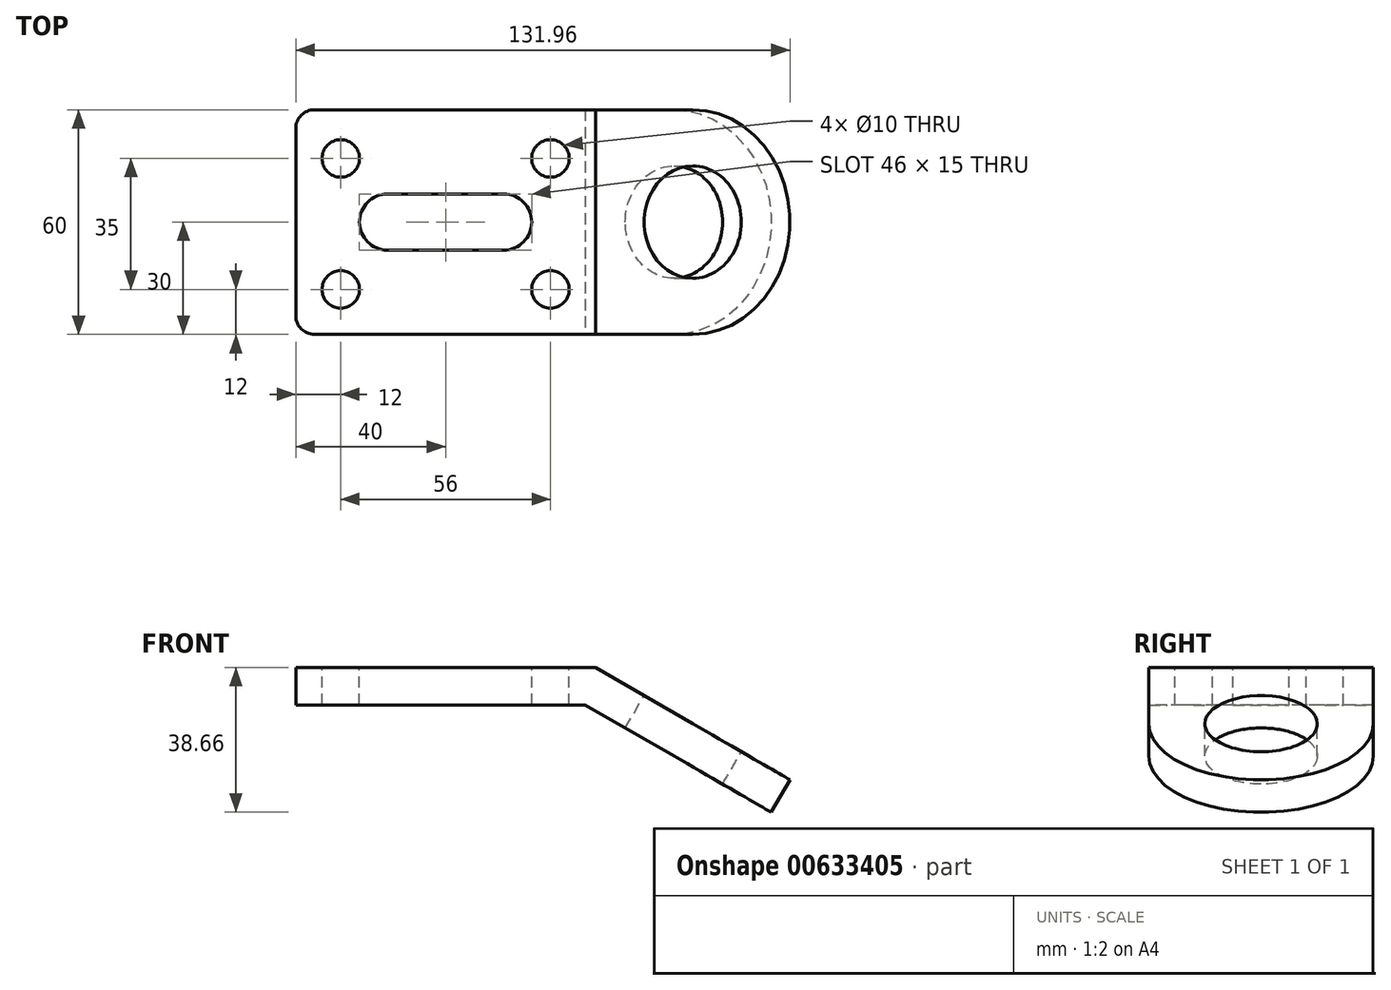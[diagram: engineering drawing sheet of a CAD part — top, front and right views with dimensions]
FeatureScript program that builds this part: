
annotation { "Feature Type Name" : "Feature", "Feature Type Description" : "" }
export const myFeature = defineFeature(function(context is Context, id is Id, definition is map)
    precondition{}
    {
        {
            var Q0;
            Q0=qCreatedBy(makeId("Front.planeOp"),FACE);
            var sketch = newSketch(context, id + "F0", { "sketchPlane" : qUnion([Q0])});
            skLineSegment(sketch, "E0", {"start": v(0, 0) * mm, "end": v(80, 0) * mm});
            skLineSegment(sketch, "E1", {"start": v(80, 0) * mm, "end": v(131.96, -30) * mm});
            skLineSegment(sketch, "E2.0", {"start": v(77.32, -10) * mm, "end": v(126.96, -38.66) * mm});
            skLineSegment(sketch, "E2.1", {"start": v(0, -10) * mm, "end": v(77.32, -10) * mm});
            skLineSegment(sketch, "E3", {"start": v(0, 0) * mm, "end": v(0, -10) * mm});
            skLineSegment(sketch, "E4", {"start": v(131.96, -30) * mm, "end": v(126.96, -38.66) * mm});
            skSolve(sketch);
        }
        {
            var Q0;
            Q0=makeQuery(id+"F0.imprint","IMPRINT",FACE,{"disambiguationData":[TD([[makeQuery(id+"F0.imprint","IMPRINT",EDGE,{"derivedFrom":sQuery(id+"F0.wireOp",EDGE,"E0")}),-1.0]])]});
            extrude(context, id + "F1", {"entities" : qUnion([Q0]), "oppositeDirection" : true, "depth" : 60 * mm, "offsetDistance" : 25 * mm});
        }
        {
            var Q0;
            Q0=makeQuery(id+"F1.opExtrude","CAP_EDGE",EDGE,{"disambiguationData":[OSD([sQuery(id+"F0.wireOp",EDGE,"E4")])],"isStart":false});
            var Q1;
            Q1=makeQuery(id+"F1.opExtrude","CAP_EDGE",EDGE,{"disambiguationData":[OSD([sQuery(id+"F0.wireOp",EDGE,"E4")])],"isStart":true});
            fillet(context, id + "F2", {"entities" : qUnion([Q0, Q1]), "radius" : 30 * mm, "tangentPropagation" : true, "allowEdgeOverflow" : false});
        }
        {
            var Q0;
            Q0=makeQuery(id+"F1.opExtrude","SWEPT_FACE",FACE,{"disambiguationData":[OSD([sQuery(id+"F0.wireOp",EDGE,"E1")])]});
            var sketch = newSketch(context, id + "F3", { "sketchPlane" : qUnion([Q0])});
            skCircle(sketch, "E5", {"center": v(99.28, 30) * mm, "radius": 15 * mm});
            skSolve(sketch);
        }
        {
            var Q0;
            Q0=makeQuery(id+"F3.imprint","IMPRINT",FACE,{"disambiguationData":[TD([[makeQuery(id+"F3.imprint","IMPRINT",EDGE,{"derivedFrom":sQuery(id+"F3.wireOp",EDGE,"E5")}),1.0]])]});
            extrude(context, id + "F4", {"entities" : qUnion([Q0]), "operationType" : NewBodyOperationType.REMOVE, "endBound" : BoundingType.UP_TO_NEXT, "oppositeDirection" : true, "depth" : 25 * mm, "offsetDistance" : 25 * mm});
        }
        {
            var Q0;
            Q0=makeQuery(id+"F1.opExtrude","SWEPT_FACE",FACE,{"disambiguationData":[OSD([sQuery(id+"F0.wireOp",EDGE,"E0")])]});
            var sketch = newSketch(context, id + "F5", { "sketchPlane" : qUnion([Q0])});
            skCircle(sketch, "E6", {"center": v(12, 12) * mm, "radius": 5 * mm});
            skCircle(sketch, "E7.0.1.0", {"center": v(12, 47) * mm, "radius": 5 * mm});
            skCircle(sketch, "E7.1.0.0", {"center": v(68, 12) * mm, "radius": 5 * mm});
            skCircle(sketch, "E7.1.1.0", {"center": v(68, 47) * mm, "radius": 5 * mm});
            skLineSegment(sketch, "E7.direction1", {"start": v(12, 12) * mm, "end": v(68, 12) * mm, "construction": true});
            skLineSegment(sketch, "E7.direction2", {"start": v(12, 12) * mm, "end": v(12, 47) * mm, "construction": true});
            skSolve(sketch);
        }
        {
            var Q0;
            Q0=makeQuery(id+"F5.imprint","IMPRINT",FACE,{"disambiguationData":[TD([[makeQuery(id+"F5.imprint","IMPRINT",EDGE,{"derivedFrom":sQuery(id+"F5.wireOp",EDGE,"E7.0.1.0")}),1.0]])]});
            var Q1;
            Q1=makeQuery(id+"F5.imprint","IMPRINT",FACE,{"disambiguationData":[TD([[makeQuery(id+"F5.imprint","IMPRINT",EDGE,{"derivedFrom":sQuery(id+"F5.wireOp",EDGE,"E6")}),1.0]])]});
            var Q2;
            Q2=makeQuery(id+"F5.imprint","IMPRINT",FACE,{"disambiguationData":[TD([[makeQuery(id+"F5.imprint","IMPRINT",EDGE,{"derivedFrom":sQuery(id+"F5.wireOp",EDGE,"E7.1.0.0")}),1.0]])]});
            var Q3;
            Q3=makeQuery(id+"F5.imprint","IMPRINT",FACE,{"disambiguationData":[TD([[makeQuery(id+"F5.imprint","IMPRINT",EDGE,{"derivedFrom":sQuery(id+"F5.wireOp",EDGE,"E7.1.1.0")}),1.0]])]});
            extrude(context, id + "F6", {"entities" : qUnion([Q0, Q1, Q2, Q3]), "operationType" : NewBodyOperationType.REMOVE, "endBound" : BoundingType.UP_TO_NEXT, "oppositeDirection" : true, "depth" : 25 * mm, "offsetDistance" : 25 * mm});
        }
        {
            var Q0;
            Q0=makeQuery(id+"F1.opExtrude","SWEPT_FACE",FACE,{"disambiguationData":[OSD([sQuery(id+"F0.wireOp",EDGE,"E0")])]});
            var sketch = newSketch(context, id + "F7", { "sketchPlane" : qUnion([Q0])});
            skLineSegment(sketch, "E8.bottom", {"start": v(24.5, 37.5) * mm, "end": v(55.5, 37.5) * mm});
            skLineSegment(sketch, "E8.top", {"start": v(24.5, 22.5) * mm, "end": v(55.5, 22.5) * mm});
            skLineSegment(sketch, "E8.left", {"start": v(17, 30) * mm, "end": v(17, 30) * mm});
            skLineSegment(sketch, "E8.right", {"start": v(63, 30) * mm, "end": v(63, 30) * mm});
            skPoint(sketch, "E8.middle", {"position": v(40, 30) * mm});
            skPoint(sketch, "E8.middle.positionSnap0", {"position": v(0, 30) * mm});
            skPoint(sketch, "E8.middle.positionSnap1", {"position": v(40, 60) * mm});
            skPoint(sketch, "E8.centerSnap0", {"position": v(0, 30) * mm});
            skPoint(sketch, "E8.centerSnap1", {"position": v(40, 60) * mm});
            skPoint(sketch, "E9.visualSharp", {"position": v(17, 37.5) * mm});
            skArc(sketch, "E9.filletArc", {"start": v(24.5, 37.5) * mm, "mid": v(19.2, 35.3) * mm, "end": v(17, 30) * mm});
            skPoint(sketch, "E10.visualSharp", {"position": v(17, 22.5) * mm});
            skArc(sketch, "E10.filletArc", {"start": v(17, 30) * mm, "mid": v(19.2, 24.7) * mm, "end": v(24.5, 22.5) * mm});
            skPoint(sketch, "E11.visualSharp", {"position": v(63, 22.5) * mm});
            skArc(sketch, "E11.filletArc", {"start": v(55.5, 22.5) * mm, "mid": v(60.8, 24.7) * mm, "end": v(63, 30) * mm});
            skPoint(sketch, "E12.visualSharp", {"position": v(63, 37.5) * mm});
            skArc(sketch, "E12.filletArc", {"start": v(63, 30) * mm, "mid": v(60.8, 35.3) * mm, "end": v(55.5, 37.5) * mm});
            skSolve(sketch);
        }
        {
            var Q0;
            Q0=makeQuery(id+"F7.imprint","IMPRINT",FACE,{"disambiguationData":[TD([[makeQuery(id+"F7.imprint","IMPRINT",EDGE,{"derivedFrom":sQuery(id+"F7.wireOp",EDGE,"E8.bottom")}),-1.0]])]});
            extrude(context, id + "F8", {"entities" : qUnion([Q0]), "operationType" : NewBodyOperationType.REMOVE, "endBound" : BoundingType.UP_TO_NEXT, "oppositeDirection" : true, "depth" : 25 * mm, "offsetDistance" : 25 * mm});
        }
        {
            var Q0;
            Q0=makeQuery(id+"F1.opExtrude","CAP_EDGE",EDGE,{"disambiguationData":[OSD([sQuery(id+"F0.wireOp",EDGE,"E3")])],"isStart":false});
            var Q1;
            Q1=makeQuery(id+"F1.opExtrude","CAP_EDGE",EDGE,{"disambiguationData":[OSD([sQuery(id+"F0.wireOp",EDGE,"E3")])],"isStart":true});
            fillet(context, id + "F9", {"entities" : qUnion([Q0, Q1]), "radius" : 5 * mm, "tangentPropagation" : true, "allowEdgeOverflow" : false});
        }
    });
